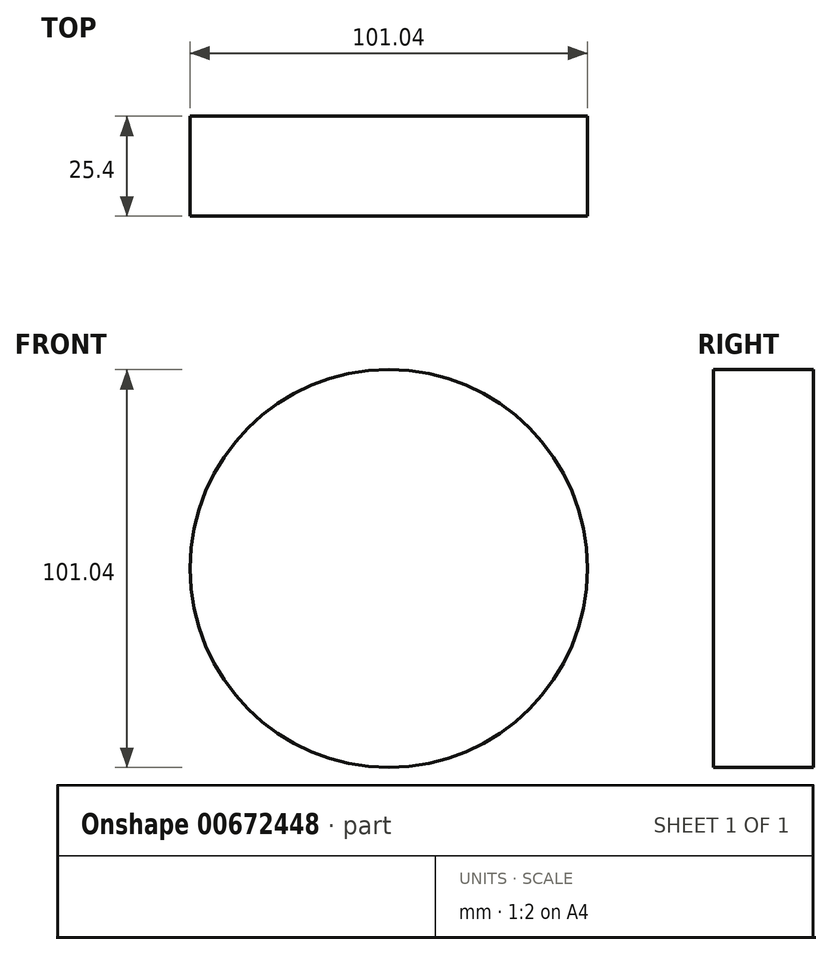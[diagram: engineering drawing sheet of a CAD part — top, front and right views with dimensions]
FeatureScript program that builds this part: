
annotation { "Feature Type Name" : "Feature", "Feature Type Description" : "" }
export const myFeature = defineFeature(function(context is Context, id is Id, definition is map)
    precondition{}
    {
        {
            var Q0;
            Q0=qCreatedBy(makeId("Front.planeOp"),FACE);
            var sketch = newSketch(context, id + "F0", { "sketchPlane" : qUnion([Q0])});
            skCircle(sketch, "E0", {"center": v(30.32, 13.08) * mm, "radius": 50.52 * mm});
            skSolve(sketch);
        }
        {
            var Q0;
            Q0 = qSketchRegion(id + "F0", true);
            extrude(context, id + "F1", {"entities" : qUnion([Q0]), "depth" : 25.4 * mm, "offsetDistance" : 25.4 * mm});
        }
    });
